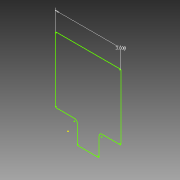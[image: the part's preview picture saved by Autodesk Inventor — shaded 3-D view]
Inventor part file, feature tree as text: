
AUTODESK INVENTOR PART (.ipt)
format: ipt  version: 2013 SP2 (Build 170200200, 200)  size: 105,984 bytes
history: native  units: in
note: dims shown in document units (in); Inventor stores cm internally (conversion verified against a paired STEP export)
features: sketch x1
ambient origin geometry x8: Origin, YZ Plane, XZ Plane, XY Plane, X Axis, Y Axis, Z Axis, Center Point
feature tree (1):
  sketch  "Sketch1"  dims[d0=3.0in]
